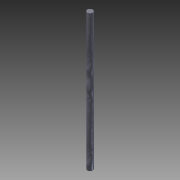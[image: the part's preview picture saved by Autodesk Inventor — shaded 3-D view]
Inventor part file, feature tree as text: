
AUTODESK INVENTOR PART (.ipt)
format: ipt  version: 2015 (Build 190159000, 159)  size: 86,016 bytes
history: native  units: mm
features: other x1, extrude x1, sketch x1
ambient origin geometry x8: Origin, YZ Plane, XZ Plane, XY Plane, X Axis, Y Axis, Z Axis, Center Point
bodies: Body1 (feature_tree)
feature tree (3):
  other  "ソリッド1"
  extrude  "押し出し1"  Depth=3.0mm
  sketch  "スケッチ1"
